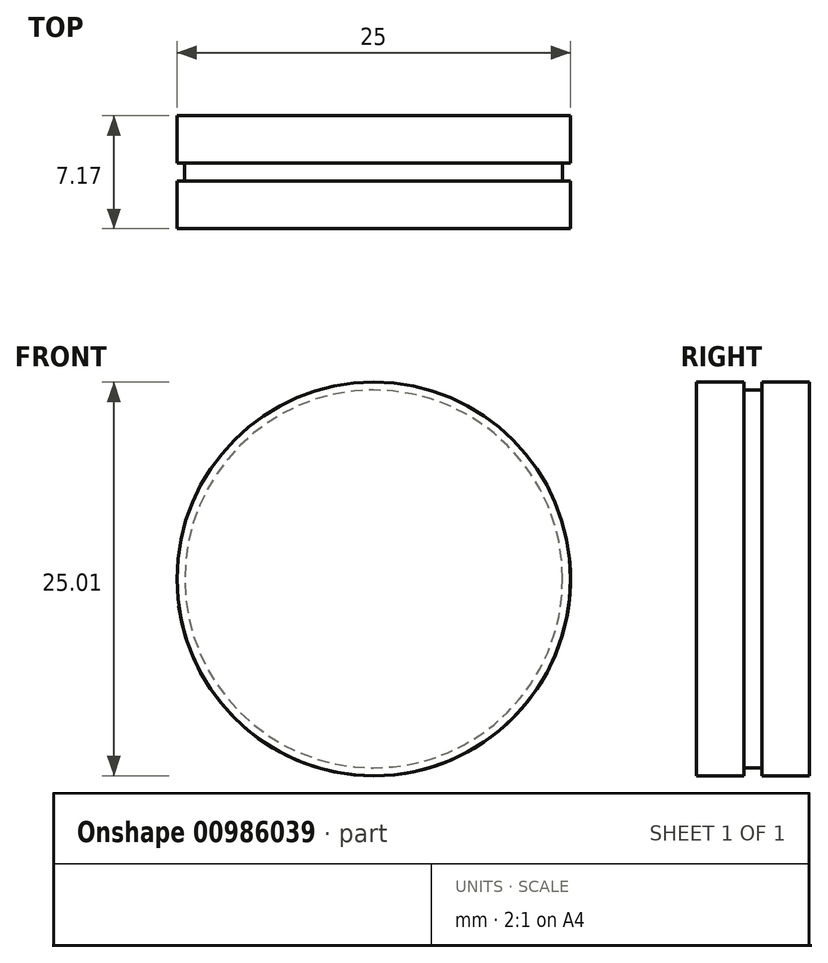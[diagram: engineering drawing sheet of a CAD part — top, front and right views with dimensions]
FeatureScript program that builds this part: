
annotation { "Feature Type Name" : "Feature", "Feature Type Description" : "" }
export const myFeature = defineFeature(function(context is Context, id is Id, definition is map)
    precondition{}
    {
        {
            var Q0;
            Q0=qCreatedBy(makeId("Front.planeOp"),FACE);
            var sketch = newSketch(context, id + "F0", { "sketchPlane" : qUnion([Q0])});
            skCircle(sketch, "E0", {"center": v(-49, 23.24) * mm, "radius": 12.5 * mm});
            skSolve(sketch);
        }
        {
            var Q0;
            Q0=qSketchRegion(id+"F0",true);
            extrude(context, id + "F1", {"entities" : qUnion([Q0]), "depth" : 3 * mm, "offsetDistance" : 25 * mm});
        }
        {
            var Q0;
            Q0=makeQuery(id+"F1.opExtrude","CAP_FACE",FACE,{"disambiguationData":[OSD([sQuery(id+"F0.wireOp",EDGE,"E0")])],"isStart":false});
            var sketch = newSketch(context, id + "F2", { "sketchPlane" : qUnion([Q0])});
            skCircle(sketch, "E1", {"center": v(-49, 23.25) * mm, "radius": 12 * mm});
            skSolve(sketch);
        }
        {
            var Q0;
            Q0=makeQuery(id+"F2.imprint","IMPRINT",FACE,{"disambiguationData":[TD([[makeQuery(id+"F2.imprint","IMPRINT",EDGE,{"derivedFrom":sQuery(id+"F2.wireOp",EDGE,"E1")}),1.0]])]});
            extrude(context, id + "F3", {"entities" : qUnion([Q0]), "operationType" : NewBodyOperationType.ADD, "depth" : 1.67 * mm, "offsetDistance" : 25 * mm});
        }
        {
            var Q0;
            Q0=makeQuery(id+"F3.opExtrude","CAP_FACE",FACE,{"disambiguationData":[OSD([sQuery(id+"F2.wireOp",EDGE,"E1")])],"isStart":false});
            var sketch = newSketch(context, id + "F4", { "sketchPlane" : qUnion([Q0])});
            skCircle(sketch, "E2", {"center": v(-49, 23.25) * mm, "radius": 12.5 * mm});
            skSolve(sketch);
        }
        {
            var Q0;
            Q0=makeQuery(id+"F4.imprint","IMPRINT",FACE,{"disambiguationData":[TD([[makeQuery(id+"F4.imprint","IMPRINT",EDGE,{"derivedFrom":sQuery(id+"F4.wireOp",EDGE,"E2")}),1.0]])]});
            var Q1;
            Q1=makeQuery(id+"F4.imprint","IMPRINT",FACE,{"disambiguationData":[TD([[makeQuery(id+"F4.imprint","IMPRINT",EDGE,{"derivedFrom":makeQuery(id+"F3.opExtrude","CAP_EDGE",EDGE,{"disambiguationData":[OSD([sQuery(id+"F2.wireOp",EDGE,"E1")])],"isStart":false})}),1.0]])]});
            extrude(context, id + "F5", {"entities" : qUnion([Q0, Q1]), "operationType" : NewBodyOperationType.ADD, "depth" : 2.5 * mm, "offsetDistance" : 25 * mm, "hasSecondDirection" : true, "secondDirectionOppositeDirection" : true, "secondDirectionDepth" : 0.5 * mm});
        }
    });
